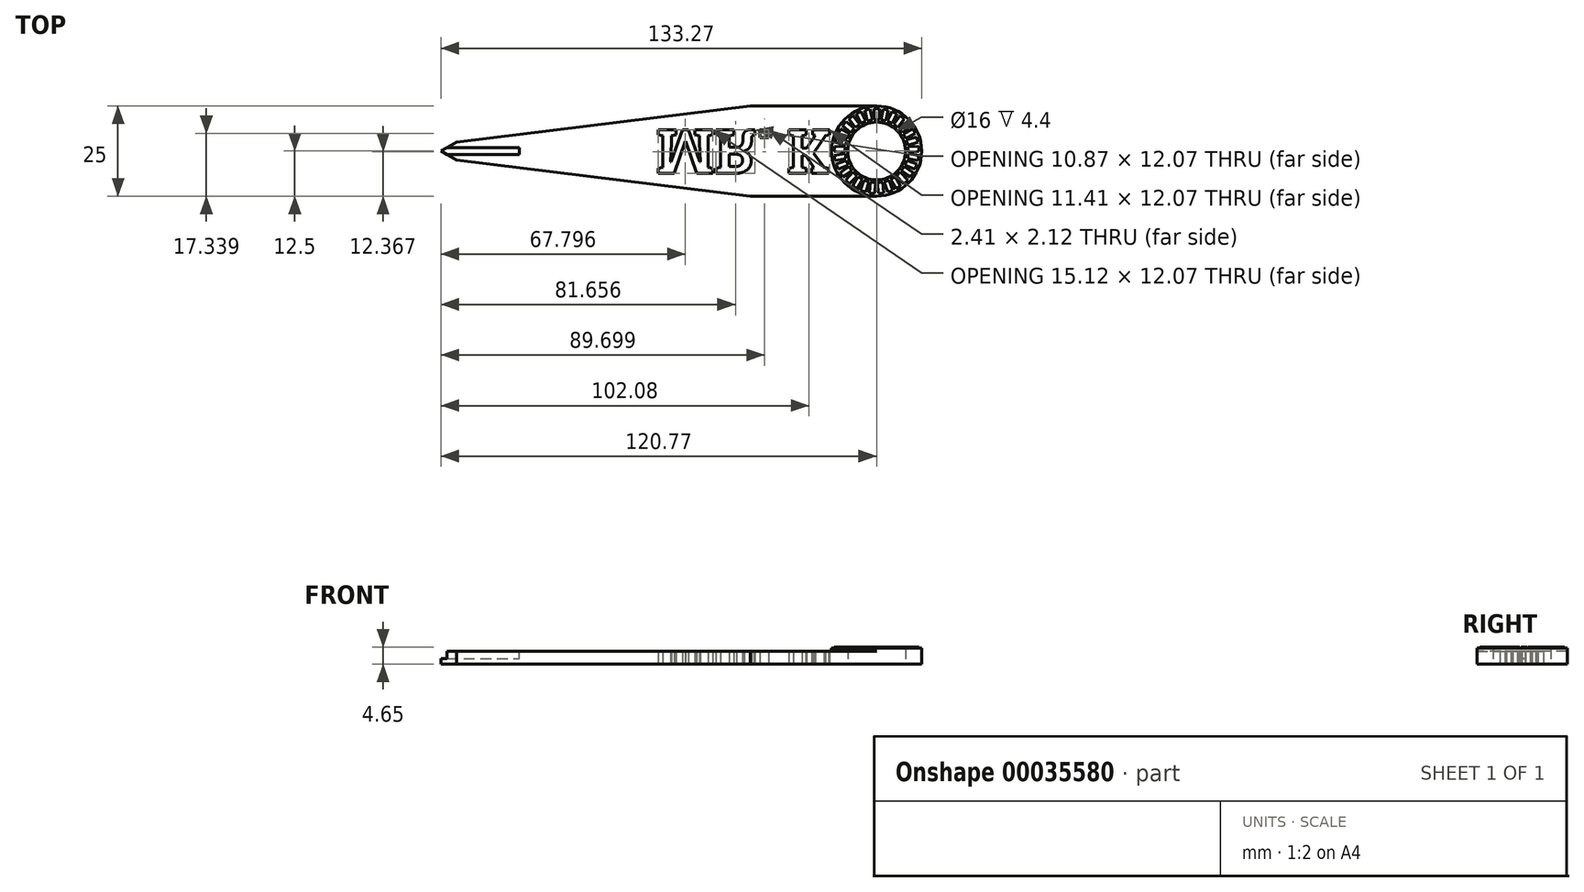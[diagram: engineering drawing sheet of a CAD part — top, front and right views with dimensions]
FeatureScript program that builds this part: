
annotation { "Feature Type Name" : "Feature", "Feature Type Description" : "" }
export const myFeature = defineFeature(function(context is Context, id is Id, definition is map)
    precondition{}
    {
        {
            var Q0;
            Q0=qCreatedBy(makeId("Top.planeOp"),FACE);
            var sketch = newSketch(context, id + "F0", { "sketchPlane" : qUnion([Q0])});
            skCircle(sketch, "E0", {"center": v(0, 0) * mm, "radius": 8 * mm});
            skCircle(sketch, "E1", {"center": v(0, 0) * mm, "radius": 12.5 * mm});
            skLineSegment(sketch, "E2", {"start": v(-35, 12.5) * mm, "end": v(0, 12.5) * mm});
            skLineSegment(sketch, "E3", {"start": v(-35, -12.5) * mm, "end": v(0, -12.5) * mm});
            skLineSegment(sketch, "E4", {"start": v(-35, 12.5) * mm, "end": v(-122.63, 12.5) * mm, "construction": true});
            skLineSegment(sketch, "E5", {"start": v(-35, 12.5) * mm, "end": v(-116.39, 2.5) * mm});
            skLineSegment(sketch, "E6", {"start": v(-35, -12.5) * mm, "end": v(-124.23, -12.5) * mm, "construction": true});
            skLineSegment(sketch, "E7", {"start": v(-35, -12.5) * mm, "end": v(-116.39, -2.5) * mm});
            skLineSegment(sketch, "E8", {"start": v(-116.39, 2.5) * mm, "end": v(-116.39, -2.5) * mm});
            skLineSegment(sketch, "E9", {"start": v(-120.77, 0) * mm, "end": v(-116.39, 2.5) * mm});
            skLineSegment(sketch, "E10", {"start": v(-120.77, 0) * mm, "end": v(-116.39, -2.5) * mm});
            skSolve(sketch);
        }
        {
            var Q0;
            Q0=qSketchRegion(id+"F0",true);
            extrude(context, id + "F1", {"entities" : qUnion([Q0]), "depth" : 3.5 * mm});
        }
        {
            var Q0;
            Q0=qCreatedBy(makeId("Top.planeOp"),FACE);
            var sketch = newSketch(context, id + "F2", { "sketchPlane" : qUnion([Q0])});
            skCircle(sketch, "E11", {"center": v(0, 0) * mm, "radius": 8 * mm});
            skCircle(sketch, "E12", {"center": v(0, 0) * mm, "radius": 12.5 * mm});
            skSolve(sketch);
        }
        {
            var Q0;
            Q0=qSketchRegion(id+"FTT6pSvakFv8IsX_1",true);
            var Q1;
            Q1=qSketchRegion(id+"F2",true);
            extrude(context, id + "F3", {"entities" : qUnion([Q0, Q1]), "operationType" : NewBodyOperationType.ADD, "depth" : 4.4 * mm});
        }
        {
            var Q0;
            Q0=makeQuery(id+"F1.opExtrude","CAP_FACE",FACE,{"disambiguationData":[OSD([sQuery(id+"F0.wireOp",EDGE,"E0"),sQuery(id+"F0.wireOp",EDGE,"E1"),sQuery(id+"F0.wireOp",EDGE,"E2"),sQuery(id+"F0.wireOp",EDGE,"E3"),sQuery(id+"F0.wireOp",EDGE,"E5"),sQuery(id+"F0.wireOp",EDGE,"E7"),sQuery(id+"F0.wireOp",EDGE,"E9"),sQuery(id+"F0.wireOp",EDGE,"E10"),sQuery(id+"F0.wireOp",EDGE,"41b71ed3-3365-47f3-8b95-72667886b5d8.sketch_text.stroke-0"),sQuery(id+"F0.wireOp",EDGE,"41b71ed3-3365-47f3-8b95-72667886b5d8.sketch_text.stroke-1"),sQuery(id+"F0.wireOp",EDGE,"41b71ed3-3365-47f3-8b95-72667886b5d8.sketch_text.stroke-2"),sQuery(id+"F0.wireOp",EDGE,"41b71ed3-3365-47f3-8b95-72667886b5d8.sketch_text.stroke-3"),sQuery(id+"F0.wireOp",EDGE,"41b71ed3-3365-47f3-8b95-72667886b5d8.sketch_text.stroke-4"),sQuery(id+"F0.wireOp",EDGE,"41b71ed3-3365-47f3-8b95-72667886b5d8.sketch_text.stroke-5"),sQuery(id+"F0.wireOp",EDGE,"41b71ed3-3365-47f3-8b95-72667886b5d8.sketch_text.stroke-6"),sQuery(id+"F0.wireOp",EDGE,"41b71ed3-3365-47f3-8b95-72667886b5d8.sketch_text.stroke-7"),sQuery(id+"F0.wireOp",EDGE,"41b71ed3-3365-47f3-8b95-72667886b5d8.sketch_text.stroke-8"),sQuery(id+"F0.wireOp",EDGE,"41b71ed3-3365-47f3-8b95-72667886b5d8.sketch_text.stroke-9"),sQuery(id+"F0.wireOp",EDGE,"41b71ed3-3365-47f3-8b95-72667886b5d8.sketch_text.stroke-10"),sQuery(id+"F0.wireOp",EDGE,"41b71ed3-3365-47f3-8b95-72667886b5d8.sketch_text.stroke-11"),sQuery(id+"F0.wireOp",EDGE,"41b71ed3-3365-47f3-8b95-72667886b5d8.sketch_text.stroke-12"),sQuery(id+"F0.wireOp",EDGE,"41b71ed3-3365-47f3-8b95-72667886b5d8.sketch_text.stroke-13"),sQuery(id+"F0.wireOp",EDGE,"41b71ed3-3365-47f3-8b95-72667886b5d8.sketch_text.stroke-14"),sQuery(id+"F0.wireOp",EDGE,"41b71ed3-3365-47f3-8b95-72667886b5d8.sketch_text.stroke-15"),sQuery(id+"F0.wireOp",EDGE,"41b71ed3-3365-47f3-8b95-72667886b5d8.sketch_text.stroke-16"),sQuery(id+"F0.wireOp",EDGE,"41b71ed3-3365-47f3-8b95-72667886b5d8.sketch_text.stroke-17"),sQuery(id+"F0.wireOp",EDGE,"41b71ed3-3365-47f3-8b95-72667886b5d8.sketch_text.stroke-18"),sQuery(id+"F0.wireOp",EDGE,"41b71ed3-3365-47f3-8b95-72667886b5d8.sketch_text.stroke-19"),sQuery(id+"F0.wireOp",EDGE,"41b71ed3-3365-47f3-8b95-72667886b5d8.sketch_text.stroke-20"),sQuery(id+"F0.wireOp",EDGE,"41b71ed3-3365-47f3-8b95-72667886b5d8.sketch_text.stroke-21"),sQuery(id+"F0.wireOp",EDGE,"41b71ed3-3365-47f3-8b95-72667886b5d8.sketch_text.stroke-22"),sQuery(id+"F0.wireOp",EDGE,"41b71ed3-3365-47f3-8b95-72667886b5d8.sketch_text.stroke-23"),sQuery(id+"F0.wireOp",EDGE,"41b71ed3-3365-47f3-8b95-72667886b5d8.sketch_text.stroke-24"),sQuery(id+"F0.wireOp",EDGE,"41b71ed3-3365-47f3-8b95-72667886b5d8.sketch_text.stroke-25"),sQuery(id+"F0.wireOp",EDGE,"41b71ed3-3365-47f3-8b95-72667886b5d8.sketch_text.stroke-26"),sQuery(id+"F0.wireOp",EDGE,"41b71ed3-3365-47f3-8b95-72667886b5d8.sketch_text.stroke-27"),sQuery(id+"F0.wireOp",EDGE,"41b71ed3-3365-47f3-8b95-72667886b5d8.sketch_text.stroke-28"),sQuery(id+"F0.wireOp",EDGE,"41b71ed3-3365-47f3-8b95-72667886b5d8.sketch_text.stroke-29"),sQuery(id+"F0.wireOp",EDGE,"41b71ed3-3365-47f3-8b95-72667886b5d8.sketch_text.stroke-30"),sQuery(id+"F0.wireOp",EDGE,"41b71ed3-3365-47f3-8b95-72667886b5d8.sketch_text.stroke-31"),sQuery(id+"F0.wireOp",EDGE,"41b71ed3-3365-47f3-8b95-72667886b5d8.sketch_text.stroke-32"),sQuery(id+"F0.wireOp",EDGE,"41b71ed3-3365-47f3-8b95-72667886b5d8.sketch_text.stroke-33"),sQuery(id+"F0.wireOp",EDGE,"41b71ed3-3365-47f3-8b95-72667886b5d8.sketch_text.stroke-34"),sQuery(id+"F0.wireOp",EDGE,"41b71ed3-3365-47f3-8b95-72667886b5d8.sketch_text.stroke-35"),sQuery(id+"F0.wireOp",EDGE,"41b71ed3-3365-47f3-8b95-72667886b5d8.sketch_text.stroke-36"),sQuery(id+"F0.wireOp",EDGE,"41b71ed3-3365-47f3-8b95-72667886b5d8.sketch_text.stroke-37"),sQuery(id+"F0.wireOp",EDGE,"41b71ed3-3365-47f3-8b95-72667886b5d8.sketch_text.stroke-38"),sQuery(id+"F0.wireOp",EDGE,"41b71ed3-3365-47f3-8b95-72667886b5d8.sketch_text.stroke-39"),sQuery(id+"F0.wireOp",EDGE,"41b71ed3-3365-47f3-8b95-72667886b5d8.sketch_text.stroke-40"),sQuery(id+"F0.wireOp",EDGE,"41b71ed3-3365-47f3-8b95-72667886b5d8.sketch_text.stroke-41"),sQuery(id+"F0.wireOp",EDGE,"41b71ed3-3365-47f3-8b95-72667886b5d8.sketch_text.stroke-42"),sQuery(id+"F0.wireOp",EDGE,"41b71ed3-3365-47f3-8b95-72667886b5d8.sketch_text.stroke-43"),sQuery(id+"F0.wireOp",EDGE,"41b71ed3-3365-47f3-8b95-72667886b5d8.sketch_text.stroke-44"),sQuery(id+"F0.wireOp",EDGE,"41b71ed3-3365-47f3-8b95-72667886b5d8.sketch_text.stroke-45"),sQuery(id+"F0.wireOp",EDGE,"41b71ed3-3365-47f3-8b95-72667886b5d8.sketch_text.stroke-46"),sQuery(id+"F0.wireOp",EDGE,"41b71ed3-3365-47f3-8b95-72667886b5d8.sketch_text.stroke-47"),sQuery(id+"F0.wireOp",EDGE,"41b71ed3-3365-47f3-8b95-72667886b5d8.sketch_text.stroke-48"),sQuery(id+"F0.wireOp",EDGE,"41b71ed3-3365-47f3-8b95-72667886b5d8.sketch_text.stroke-49"),sQuery(id+"F0.wireOp",EDGE,"41b71ed3-3365-47f3-8b95-72667886b5d8.sketch_text.stroke-50"),sQuery(id+"F0.wireOp",EDGE,"41b71ed3-3365-47f3-8b95-72667886b5d8.sketch_text.stroke-51"),sQuery(id+"F0.wireOp",EDGE,"41b71ed3-3365-47f3-8b95-72667886b5d8.sketch_text.stroke-52"),sQuery(id+"F0.wireOp",EDGE,"41b71ed3-3365-47f3-8b95-72667886b5d8.sketch_text.stroke-53"),sQuery(id+"F0.wireOp",EDGE,"41b71ed3-3365-47f3-8b95-72667886b5d8.sketch_text.stroke-54"),sQuery(id+"F0.wireOp",EDGE,"41b71ed3-3365-47f3-8b95-72667886b5d8.sketch_text.stroke-55"),sQuery(id+"F0.wireOp",EDGE,"41b71ed3-3365-47f3-8b95-72667886b5d8.sketch_text.stroke-56"),sQuery(id+"F0.wireOp",EDGE,"41b71ed3-3365-47f3-8b95-72667886b5d8.sketch_text.stroke-57"),sQuery(id+"F0.wireOp",EDGE,"41b71ed3-3365-47f3-8b95-72667886b5d8.sketch_text.stroke-58"),sQuery(id+"F0.wireOp",EDGE,"41b71ed3-3365-47f3-8b95-72667886b5d8.sketch_text.stroke-59"),sQuery(id+"F0.wireOp",EDGE,"41b71ed3-3365-47f3-8b95-72667886b5d8.sketch_text.stroke-67"),sQuery(id+"F0.wireOp",EDGE,"41b71ed3-3365-47f3-8b95-72667886b5d8.sketch_text.stroke-68"),sQuery(id+"F0.wireOp",EDGE,"41b71ed3-3365-47f3-8b95-72667886b5d8.sketch_text.stroke-69"),sQuery(id+"F0.wireOp",EDGE,"41b71ed3-3365-47f3-8b95-72667886b5d8.sketch_text.stroke-70"),sQuery(id+"F0.wireOp",EDGE,"41b71ed3-3365-47f3-8b95-72667886b5d8.sketch_text.stroke-71"),sQuery(id+"F0.wireOp",EDGE,"41b71ed3-3365-47f3-8b95-72667886b5d8.sketch_text.stroke-72"),sQuery(id+"F0.wireOp",EDGE,"41b71ed3-3365-47f3-8b95-72667886b5d8.sketch_text.stroke-73"),sQuery(id+"F0.wireOp",EDGE,"41b71ed3-3365-47f3-8b95-72667886b5d8.sketch_text.stroke-74"),sQuery(id+"F0.wireOp",EDGE,"41b71ed3-3365-47f3-8b95-72667886b5d8.sketch_text.stroke-75"),sQuery(id+"F0.wireOp",EDGE,"41b71ed3-3365-47f3-8b95-72667886b5d8.sketch_text.stroke-76"),sQuery(id+"F0.wireOp",EDGE,"41b71ed3-3365-47f3-8b95-72667886b5d8.sketch_text.stroke-77"),sQuery(id+"F0.wireOp",EDGE,"41b71ed3-3365-47f3-8b95-72667886b5d8.sketch_text.stroke-78"),sQuery(id+"F0.wireOp",EDGE,"41b71ed3-3365-47f3-8b95-72667886b5d8.sketch_text.stroke-79"),sQuery(id+"F0.wireOp",EDGE,"41b71ed3-3365-47f3-8b95-72667886b5d8.sketch_text.stroke-80"),sQuery(id+"F0.wireOp",EDGE,"41b71ed3-3365-47f3-8b95-72667886b5d8.sketch_text.stroke-81"),sQuery(id+"F0.wireOp",EDGE,"41b71ed3-3365-47f3-8b95-72667886b5d8.sketch_text.stroke-82"),sQuery(id+"F0.wireOp",EDGE,"41b71ed3-3365-47f3-8b95-72667886b5d8.sketch_text.stroke-83"),sQuery(id+"F0.wireOp",EDGE,"41b71ed3-3365-47f3-8b95-72667886b5d8.sketch_text.stroke-84"),sQuery(id+"F0.wireOp",EDGE,"41b71ed3-3365-47f3-8b95-72667886b5d8.sketch_text.stroke-85"),sQuery(id+"F0.wireOp",EDGE,"41b71ed3-3365-47f3-8b95-72667886b5d8.sketch_text.stroke-86"),sQuery(id+"F0.wireOp",EDGE,"41b71ed3-3365-47f3-8b95-72667886b5d8.sketch_text.stroke-87"),sQuery(id+"F0.wireOp",EDGE,"41b71ed3-3365-47f3-8b95-72667886b5d8.sketch_text.stroke-88"),sQuery(id+"F0.wireOp",EDGE,"41b71ed3-3365-47f3-8b95-72667886b5d8.sketch_text.stroke-89"),sQuery(id+"F0.wireOp",EDGE,"41b71ed3-3365-47f3-8b95-72667886b5d8.sketch_text.stroke-90"),sQuery(id+"F0.wireOp",EDGE,"41b71ed3-3365-47f3-8b95-72667886b5d8.sketch_text.stroke-91"),sQuery(id+"F0.wireOp",EDGE,"41b71ed3-3365-47f3-8b95-72667886b5d8.sketch_text.stroke-92"),sQuery(id+"F0.wireOp",EDGE,"41b71ed3-3365-47f3-8b95-72667886b5d8.sketch_text.stroke-93"),sQuery(id+"F0.wireOp",EDGE,"41b71ed3-3365-47f3-8b95-72667886b5d8.sketch_text.stroke-94"),sQuery(id+"F0.wireOp",EDGE,"41b71ed3-3365-47f3-8b95-72667886b5d8.sketch_text.stroke-95"),sQuery(id+"F0.wireOp",EDGE,"41b71ed3-3365-47f3-8b95-72667886b5d8.sketch_text.stroke-96"),sQuery(id+"F0.wireOp",EDGE,"41b71ed3-3365-47f3-8b95-72667886b5d8.sketch_text.stroke-97"),sQuery(id+"F0.wireOp",EDGE,"41b71ed3-3365-47f3-8b95-72667886b5d8.sketch_text.stroke-98"),sQuery(id+"F0.wireOp",EDGE,"41b71ed3-3365-47f3-8b95-72667886b5d8.sketch_text.stroke-99")])],"isStart":false});
            var sketch = newSketch(context, id + "F4", { "sketchPlane" : qUnion([Q0])});
            skLineSegment(sketch, "E13", {"start": v(-120.77, 0) * mm, "end": v(-119.02, 1) * mm});
            skLineSegment(sketch, "E14", {"start": v(-119.02, 1) * mm, "end": v(-99.02, 1) * mm});
            skLineSegment(sketch, "E15", {"start": v(-99.02, 1) * mm, "end": v(-99.02, -1) * mm});
            skLineSegment(sketch, "E16", {"start": v(-99.02, -1) * mm, "end": v(-119.02, -1) * mm});
            skLineSegment(sketch, "E17", {"start": v(-119.02, -1) * mm, "end": v(-120.77, 0) * mm});
            skSolve(sketch);
        }
        {
            var Q0;
            Q0=qSketchRegion(id+"F4",true);
            extrude(context, id + "F5", {"entities" : qUnion([Q0]), "operationType" : NewBodyOperationType.REMOVE, "oppositeDirection" : true, "depth" : 2 * mm});
        }
        {
            var Q0;
            Q0=makeQuery(id+"F3.opExtrude","CAP_FACE",FACE,{"disambiguationData":[OSD([sQuery(id+"F2.wireOp",EDGE,"E11"),sQuery(id+"F2.wireOp",EDGE,"E12")])],"isStart":false});
            var sketch = newSketch(context, id + "F6", { "sketchPlane" : qUnion([Q0])});
            skLineSegment(sketch, "E18.bottom", {"start": v(-0.75, 11.75) * mm, "end": v(0.75, 11.75) * mm});
            skLineSegment(sketch, "E18.top", {"start": v(-0.75, 8.75) * mm, "end": v(0.75, 8.75) * mm});
            skLineSegment(sketch, "E18.left", {"start": v(-0.75, 11.75) * mm, "end": v(-0.75, 8.75) * mm});
            skLineSegment(sketch, "E18.right", {"start": v(0.75, 11.75) * mm, "end": v(0.75, 8.75) * mm});
            skLineSegment(sketch, "E19.1.0", {"start": v(3.26, 11.31) * mm, "end": v(2.61, 8.38) * mm});
            skLineSegment(sketch, "E19.1.1", {"start": v(1.15, 8.7) * mm, "end": v(2.61, 8.38) * mm});
            skLineSegment(sketch, "E19.1.2", {"start": v(1.8, 11.64) * mm, "end": v(1.15, 8.7) * mm});
            skLineSegment(sketch, "E19.1.3", {"start": v(1.8, 11.64) * mm, "end": v(3.26, 11.31) * mm});
            skLineSegment(sketch, "E19.2.0", {"start": v(5.61, 10.35) * mm, "end": v(4.35, 7.63) * mm});
            skLineSegment(sketch, "E19.2.1", {"start": v(3, 8.26) * mm, "end": v(4.35, 7.63) * mm});
            skLineSegment(sketch, "E19.2.2", {"start": v(4.25, 10.98) * mm, "end": v(3, 8.26) * mm});
            skLineSegment(sketch, "E19.2.3", {"start": v(4.25, 10.98) * mm, "end": v(5.61, 10.35) * mm});
            skLineSegment(sketch, "E19.3.0", {"start": v(7.7, 8.9) * mm, "end": v(5.9, 6.51) * mm});
            skLineSegment(sketch, "E19.3.1", {"start": v(4.7, 7.42) * mm, "end": v(5.9, 6.51) * mm});
            skLineSegment(sketch, "E19.3.2", {"start": v(6.51, 9.8) * mm, "end": v(4.7, 7.42) * mm});
            skLineSegment(sketch, "E19.3.3", {"start": v(6.51, 9.8) * mm, "end": v(7.7, 8.9) * mm});
            skLineSegment(sketch, "E19.4.0", {"start": v(9.44, 7.04) * mm, "end": v(7.15, 5.1) * mm});
            skLineSegment(sketch, "E19.4.1", {"start": v(6.18, 6.24) * mm, "end": v(7.15, 5.1) * mm});
            skLineSegment(sketch, "E19.4.2", {"start": v(8.47, 8.18) * mm, "end": v(6.18, 6.24) * mm});
            skLineSegment(sketch, "E19.4.3", {"start": v(8.47, 8.18) * mm, "end": v(9.44, 7.04) * mm});
            skLineSegment(sketch, "E19.5.0", {"start": v(10.73, 4.84) * mm, "end": v(8.08, 3.44) * mm});
            skLineSegment(sketch, "E19.5.1", {"start": v(7.38, 4.76) * mm, "end": v(8.08, 3.44) * mm});
            skLineSegment(sketch, "E19.5.2", {"start": v(10.03, 6.17) * mm, "end": v(7.38, 4.76) * mm});
            skLineSegment(sketch, "E19.5.3", {"start": v(10.03, 6.17) * mm, "end": v(10.73, 4.84) * mm});
            skLineSegment(sketch, "E19.6.0", {"start": v(11.52, 2.42) * mm, "end": v(8.63, 1.62) * mm});
            skLineSegment(sketch, "E19.6.1", {"start": v(8.23, 3.06) * mm, "end": v(8.63, 1.62) * mm});
            skLineSegment(sketch, "E19.6.2", {"start": v(11.12, 3.87) * mm, "end": v(8.23, 3.06) * mm});
            skLineSegment(sketch, "E19.6.3", {"start": v(11.12, 3.87) * mm, "end": v(11.52, 2.42) * mm});
            skLineSegment(sketch, "E19.7.0", {"start": v(11.77, -0.11) * mm, "end": v(8.78, -0.28) * mm});
            skLineSegment(sketch, "E19.7.1", {"start": v(8.7, 1.22) * mm, "end": v(8.78, -0.28) * mm});
            skLineSegment(sketch, "E19.7.2", {"start": v(11.7, 1.39) * mm, "end": v(8.7, 1.22) * mm});
            skLineSegment(sketch, "E19.7.3", {"start": v(11.7, 1.39) * mm, "end": v(11.77, -0.11) * mm});
            skLineSegment(sketch, "E19.8.0", {"start": v(11.47, -2.64) * mm, "end": v(8.51, -2.16) * mm});
            skLineSegment(sketch, "E19.8.1", {"start": v(8.76, -0.68) * mm, "end": v(8.51, -2.16) * mm});
            skLineSegment(sketch, "E19.8.2", {"start": v(11.72, -1.16) * mm, "end": v(8.76, -0.68) * mm});
            skLineSegment(sketch, "E19.8.3", {"start": v(11.72, -1.16) * mm, "end": v(11.47, -2.64) * mm});
            skLineSegment(sketch, "E19.9.0", {"start": v(10.64, -5.05) * mm, "end": v(7.85, -3.94) * mm});
            skLineSegment(sketch, "E19.9.1", {"start": v(8.4, -2.54) * mm, "end": v(7.85, -3.94) * mm});
            skLineSegment(sketch, "E19.9.2", {"start": v(11.2, -3.65) * mm, "end": v(8.4, -2.54) * mm});
            skLineSegment(sketch, "E19.9.3", {"start": v(11.2, -3.65) * mm, "end": v(10.64, -5.05) * mm});
            skLineSegment(sketch, "E19.10.0", {"start": v(9.3, -7.21) * mm, "end": v(6.82, -5.53) * mm});
            skLineSegment(sketch, "E19.10.1", {"start": v(7.66, -4.29) * mm, "end": v(6.82, -5.53) * mm});
            skLineSegment(sketch, "E19.10.2", {"start": v(10.15, -5.97) * mm, "end": v(7.66, -4.29) * mm});
            skLineSegment(sketch, "E19.10.3", {"start": v(10.15, -5.97) * mm, "end": v(9.3, -7.21) * mm});
            skLineSegment(sketch, "E19.11.0", {"start": v(7.54, -9.05) * mm, "end": v(5.47, -6.87) * mm});
            skLineSegment(sketch, "E19.11.1", {"start": v(6.56, -5.84) * mm, "end": v(5.47, -6.87) * mm});
            skLineSegment(sketch, "E19.11.2", {"start": v(8.62, -8.01) * mm, "end": v(6.56, -5.84) * mm});
            skLineSegment(sketch, "E19.11.3", {"start": v(8.62, -8.01) * mm, "end": v(7.54, -9.05) * mm});
            skLineSegment(sketch, "E19.12.0", {"start": v(5.42, -10.45) * mm, "end": v(3.87, -7.88) * mm});
            skLineSegment(sketch, "E19.12.1", {"start": v(5.15, -7.11) * mm, "end": v(3.87, -7.88) * mm});
            skLineSegment(sketch, "E19.12.2", {"start": v(6.7, -9.68) * mm, "end": v(5.15, -7.11) * mm});
            skLineSegment(sketch, "E19.12.3", {"start": v(5.42, -10.45) * mm, "end": v(6.7, -9.68) * mm});
            skLineSegment(sketch, "E19.13.0", {"start": v(3.04, -11.37) * mm, "end": v(2.08, -8.53) * mm});
            skLineSegment(sketch, "E19.13.1", {"start": v(3.5, -8.05) * mm, "end": v(2.08, -8.53) * mm});
            skLineSegment(sketch, "E19.13.2", {"start": v(4.46, -10.9) * mm, "end": v(3.5, -8.05) * mm});
            skLineSegment(sketch, "E19.13.3", {"start": v(4.46, -10.9) * mm, "end": v(3.04, -11.37) * mm});
            skLineSegment(sketch, "E19.14.0", {"start": v(0.52, -11.76) * mm, "end": v(0.2, -8.78) * mm});
            skLineSegment(sketch, "E19.14.1", {"start": v(1.7, -8.62) * mm, "end": v(0.2, -8.78) * mm});
            skLineSegment(sketch, "E19.14.2", {"start": v(2.02, -11.6) * mm, "end": v(1.7, -8.62) * mm});
            skLineSegment(sketch, "E19.14.3", {"start": v(2.02, -11.6) * mm, "end": v(0.52, -11.76) * mm});
            skLineSegment(sketch, "E19.15.0", {"start": v(-2.02, -11.6) * mm, "end": v(-1.7, -8.62) * mm});
            skLineSegment(sketch, "E19.15.1", {"start": v(-0.2, -8.78) * mm, "end": v(-1.7, -8.62) * mm});
            skLineSegment(sketch, "E19.15.2", {"start": v(-0.52, -11.76) * mm, "end": v(-0.2, -8.78) * mm});
            skLineSegment(sketch, "E19.15.3", {"start": v(-0.52, -11.76) * mm, "end": v(-2.02, -11.6) * mm});
            skLineSegment(sketch, "E19.16.0", {"start": v(-4.46, -10.9) * mm, "end": v(-3.5, -8.05) * mm});
            skLineSegment(sketch, "E19.16.1", {"start": v(-3.5, -8.05) * mm, "end": v(-2.08, -8.53) * mm});
            skLineSegment(sketch, "E19.16.2", {"start": v(-3.04, -11.37) * mm, "end": v(-2.08, -8.53) * mm});
            skLineSegment(sketch, "E19.16.3", {"start": v(-3.04, -11.37) * mm, "end": v(-4.46, -10.9) * mm});
            skLineSegment(sketch, "E19.17.0", {"start": v(-6.7, -9.68) * mm, "end": v(-5.15, -7.11) * mm});
            skLineSegment(sketch, "E19.17.1", {"start": v(-3.87, -7.88) * mm, "end": v(-5.15, -7.11) * mm});
            skLineSegment(sketch, "E19.17.2", {"start": v(-5.42, -10.45) * mm, "end": v(-3.87, -7.88) * mm});
            skLineSegment(sketch, "E19.17.3", {"start": v(-5.42, -10.45) * mm, "end": v(-6.7, -9.68) * mm});
            skLineSegment(sketch, "E19.18.0", {"start": v(-8.62, -8.01) * mm, "end": v(-6.56, -5.84) * mm});
            skLineSegment(sketch, "E19.18.1", {"start": v(-5.47, -6.87) * mm, "end": v(-6.56, -5.84) * mm});
            skLineSegment(sketch, "E19.18.2", {"start": v(-7.54, -9.05) * mm, "end": v(-5.47, -6.87) * mm});
            skLineSegment(sketch, "E19.18.3", {"start": v(-7.54, -9.05) * mm, "end": v(-8.62, -8.01) * mm});
            skLineSegment(sketch, "E19.19.0", {"start": v(-10.15, -5.97) * mm, "end": v(-7.66, -4.29) * mm});
            skLineSegment(sketch, "E19.19.1", {"start": v(-6.82, -5.53) * mm, "end": v(-7.66, -4.29) * mm});
            skLineSegment(sketch, "E19.19.2", {"start": v(-9.3, -7.21) * mm, "end": v(-6.82, -5.53) * mm});
            skLineSegment(sketch, "E19.19.3", {"start": v(-9.3, -7.21) * mm, "end": v(-10.15, -5.97) * mm});
            skLineSegment(sketch, "E19.20.0", {"start": v(-11.2, -3.65) * mm, "end": v(-8.4, -2.54) * mm});
            skLineSegment(sketch, "E19.20.1", {"start": v(-7.85, -3.94) * mm, "end": v(-8.4, -2.54) * mm});
            skLineSegment(sketch, "E19.20.2", {"start": v(-10.64, -5.05) * mm, "end": v(-7.85, -3.94) * mm});
            skLineSegment(sketch, "E19.20.3", {"start": v(-10.64, -5.05) * mm, "end": v(-11.2, -3.65) * mm});
            skLineSegment(sketch, "E19.21.0", {"start": v(-11.72, -1.16) * mm, "end": v(-8.76, -0.68) * mm});
            skLineSegment(sketch, "E19.21.1", {"start": v(-8.51, -2.16) * mm, "end": v(-8.76, -0.68) * mm});
            skLineSegment(sketch, "E19.21.2", {"start": v(-11.47, -2.64) * mm, "end": v(-8.51, -2.16) * mm});
            skLineSegment(sketch, "E19.21.3", {"start": v(-11.47, -2.64) * mm, "end": v(-11.72, -1.16) * mm});
            skLineSegment(sketch, "E19.22.0", {"start": v(-11.7, 1.39) * mm, "end": v(-8.7, 1.22) * mm});
            skLineSegment(sketch, "E19.22.1", {"start": v(-8.78, -0.28) * mm, "end": v(-8.7, 1.22) * mm});
            skLineSegment(sketch, "E19.22.2", {"start": v(-11.77, -0.11) * mm, "end": v(-8.78, -0.28) * mm});
            skLineSegment(sketch, "E19.22.3", {"start": v(-11.77, -0.11) * mm, "end": v(-11.7, 1.39) * mm});
            skLineSegment(sketch, "E19.23.0", {"start": v(-11.12, 3.87) * mm, "end": v(-8.23, 3.06) * mm});
            skLineSegment(sketch, "E19.23.1", {"start": v(-8.63, 1.62) * mm, "end": v(-8.23, 3.06) * mm});
            skLineSegment(sketch, "E19.23.2", {"start": v(-11.52, 2.42) * mm, "end": v(-8.63, 1.62) * mm});
            skLineSegment(sketch, "E19.23.3", {"start": v(-11.52, 2.42) * mm, "end": v(-11.12, 3.87) * mm});
            skLineSegment(sketch, "E19.24.0", {"start": v(-10.03, 6.17) * mm, "end": v(-7.38, 4.76) * mm});
            skLineSegment(sketch, "E19.24.1", {"start": v(-8.08, 3.44) * mm, "end": v(-7.38, 4.76) * mm});
            skLineSegment(sketch, "E19.24.2", {"start": v(-10.73, 4.84) * mm, "end": v(-8.08, 3.44) * mm});
            skLineSegment(sketch, "E19.24.3", {"start": v(-10.73, 4.84) * mm, "end": v(-10.03, 6.17) * mm});
            skLineSegment(sketch, "E19.25.0", {"start": v(-8.47, 8.18) * mm, "end": v(-6.18, 6.24) * mm});
            skLineSegment(sketch, "E19.25.1", {"start": v(-7.15, 5.1) * mm, "end": v(-6.18, 6.24) * mm});
            skLineSegment(sketch, "E19.25.2", {"start": v(-9.44, 7.04) * mm, "end": v(-7.15, 5.1) * mm});
            skLineSegment(sketch, "E19.25.3", {"start": v(-9.44, 7.04) * mm, "end": v(-8.47, 8.18) * mm});
            skLineSegment(sketch, "E19.26.0", {"start": v(-6.51, 9.8) * mm, "end": v(-4.7, 7.42) * mm});
            skLineSegment(sketch, "E19.26.1", {"start": v(-5.9, 6.51) * mm, "end": v(-4.7, 7.42) * mm});
            skLineSegment(sketch, "E19.26.2", {"start": v(-7.7, 8.9) * mm, "end": v(-5.9, 6.51) * mm});
            skLineSegment(sketch, "E19.26.3", {"start": v(-7.7, 8.9) * mm, "end": v(-6.51, 9.8) * mm});
            skLineSegment(sketch, "E19.27.0", {"start": v(-4.25, 10.98) * mm, "end": v(-3, 8.26) * mm});
            skLineSegment(sketch, "E19.27.1", {"start": v(-4.35, 7.63) * mm, "end": v(-3, 8.26) * mm});
            skLineSegment(sketch, "E19.27.2", {"start": v(-5.61, 10.35) * mm, "end": v(-4.35, 7.63) * mm});
            skLineSegment(sketch, "E19.27.3", {"start": v(-5.61, 10.35) * mm, "end": v(-4.25, 10.98) * mm});
            skLineSegment(sketch, "E19.28.0", {"start": v(-1.8, 11.64) * mm, "end": v(-1.15, 8.7) * mm});
            skLineSegment(sketch, "E19.28.1", {"start": v(-2.61, 8.38) * mm, "end": v(-1.15, 8.7) * mm});
            skLineSegment(sketch, "E19.28.2", {"start": v(-3.26, 11.31) * mm, "end": v(-2.61, 8.38) * mm});
            skLineSegment(sketch, "E19.28.3", {"start": v(-3.26, 11.31) * mm, "end": v(-1.8, 11.64) * mm});
            skPoint(sketch, "E19.center", {"position": v(0, 0) * mm});
            skLineSegment(sketch, "E19.anchor1", {"start": v(0, 0) * mm, "end": v(0.75, 8.75) * mm, "construction": true});
            skSolve(sketch);
        }
        {
            var Q0;
            Q0=qSketchRegion(id+"F6",true);
            extrude(context, id + "F7", {"entities" : qUnion([Q0]), "operationType" : NewBodyOperationType.ADD, "depth" : .25 * mm});
        }
        {
            var Q0;
            Q0=makeQuery(id+"F1.opExtrude","CAP_FACE",FACE,{"disambiguationData":[OSD([sQuery(id+"F0.wireOp",EDGE,"E0"),sQuery(id+"F0.wireOp",EDGE,"E1"),sQuery(id+"F0.wireOp",EDGE,"E2"),sQuery(id+"F0.wireOp",EDGE,"E3"),sQuery(id+"F0.wireOp",EDGE,"E5"),sQuery(id+"F0.wireOp",EDGE,"E7"),sQuery(id+"F0.wireOp",EDGE,"E9"),sQuery(id+"F0.wireOp",EDGE,"E10")])],"isStart":true});
            var sketch = newSketch(context, id + "F8", { "sketchPlane" : qUnion([Q0])});
            skText(sketch, "E20", { "text": "MR. K", "fontName": "RobotoSlab-Bold.ttf"});
            const initialGuessF8  = {"E20": [-0.061, -0.0059, 1, 0, 0.01222]};
            skSetInitialGuess(sketch, initialGuessF8);
            skSolve(sketch);
        }
        {
            var Q0;
            Q0=qSketchRegion(id+"F8",true);
            extrude(context, id + "F9", {"entities" : qUnion([Q0]), "operationType" : NewBodyOperationType.REMOVE, "endBound" : BoundingType.THROUGH_ALL, "oppositeDirection" : true, "depth" : 25 * mm});
        }
    });
